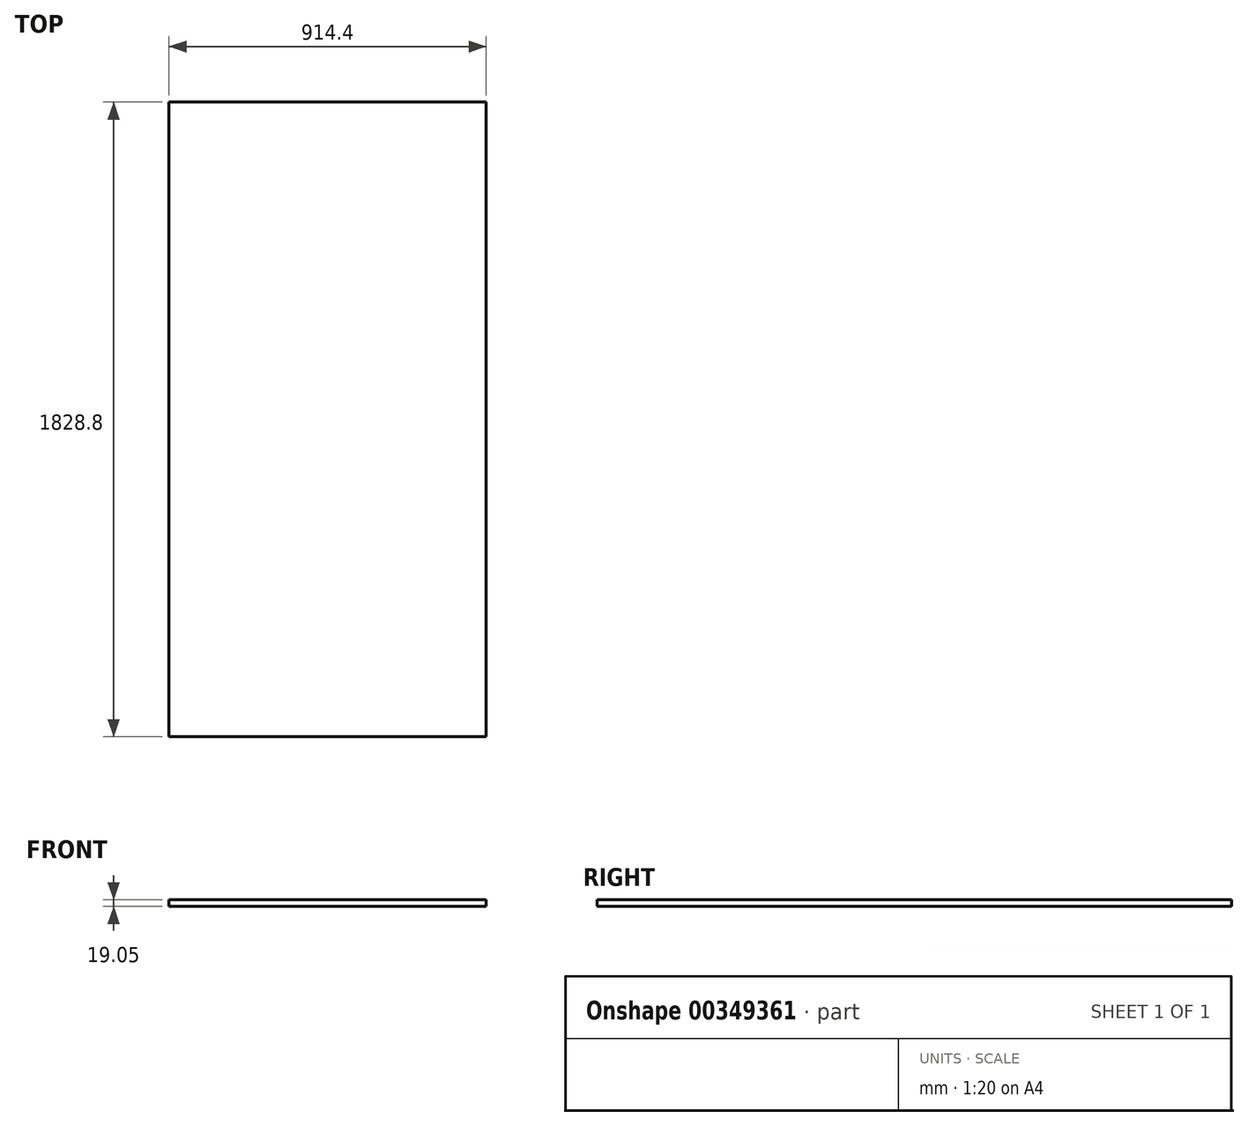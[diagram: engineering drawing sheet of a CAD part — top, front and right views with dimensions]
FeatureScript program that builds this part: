
annotation { "Feature Type Name" : "Feature", "Feature Type Description" : "" }
export const myFeature = defineFeature(function(context is Context, id is Id, definition is map)
    precondition{}
    {
        {
            var Q0;
            Q0=qCreatedBy(makeId("Top.planeOp"),FACE);
            var sketch = newSketch(context, id + "F0", { "sketchPlane" : qUnion([Q0])});
            skLineSegment(sketch, "E0.bottom", {"start": v(-504.12, 1554.88) * mm, "end": v(410.28, 1554.88) * mm});
            skLineSegment(sketch, "E0.top", {"start": v(-504.12, -273.92) * mm, "end": v(410.28, -273.92) * mm});
            skLineSegment(sketch, "E0.left", {"start": v(-504.12, 1554.88) * mm, "end": v(-504.12, -273.92) * mm});
            skLineSegment(sketch, "E0.right", {"start": v(410.28, 1554.88) * mm, "end": v(410.28, -273.92) * mm});
            skSolve(sketch);
        }
        {
            var Q0;
            Q0=makeQuery(id+"F0.imprint","IMPRINT",FACE,{"disambiguationData":[TD([[makeQuery(id+"F0.imprint","IMPRINT",EDGE,{"derivedFrom":sQuery(id+"F0.wireOp",EDGE,"E0.bottom")}),-1.0]])]});
            extrude(context, id + "F1", {"entities" : qUnion([Q0]), "depth" : 19.05 * mm});
        }
    });
